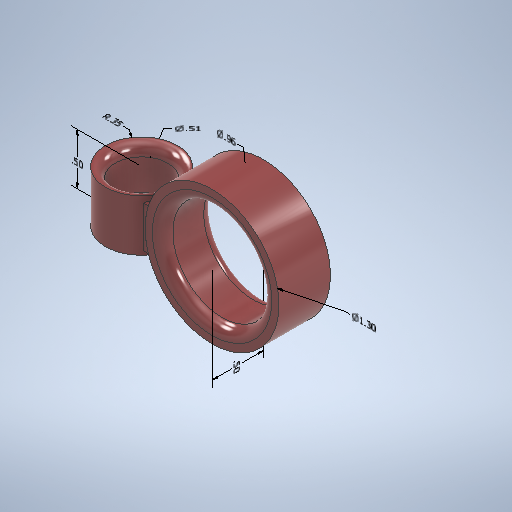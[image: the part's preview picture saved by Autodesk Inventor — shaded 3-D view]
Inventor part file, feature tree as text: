
AUTODESK INVENTOR PART (.ipt)
format: ipt  version: 2025.2 (Build 292293000, 293)  size: 366,592 bytes
history: native  units: in
note: dims shown in document units (in); Inventor stores cm internally (conversion verified against a paired STEP export)
features: other x7, sketch x4, extrude x3, plane x2, fillet x1
ambient origin geometry x8: Origin, YZ Plane, XZ Plane, XY Plane, X Axis, Y Axis, Z Axis, Center Point
bodies: Solid1 (feature_tree)
feature tree (17):
  other  "Annotations"
  extrude  "Extrusion1"  Depth=0.7in
  plane  "Work Plane1"
  sketch  "Sketch2"  dims[d2=0.5in d3=0.0in d4=1.0in d5=0.35in]
  plane  "Work Plane3"
  extrude  "Extrusion2"  Depth=0.35in
  fillet  "Fillet1"  Radius=0.35in
  extrude  "Extrusion3"  Depth=0.5in
  sketch  "Sketch1"  dims[d0=0.51in d1=0.7in]
  sketch  "Sketch5"  dims[d6=0.5in d7=0.5in]
  sketch  "Sketch6"  dims[d8=90.0deg d10=0.96in d11=0.25in d12=1.3in d13=0.5in d14=0.0in d15=0.1in d16=0.4in d17=0.0in d18=-0.57in d19=0.96in d20=0.5in d21=0.0811in d22=1.3in d23=0.7183in d24=0.51in d25=0.5in d26=2.239in d27=0.35in]
  other  "Diameter Dimension 1"
  other  "Linear Dimension 1"
  other  "Diameter Dimension 2"
  other  "Diameter Dimension 3"
  other  "Linear Dimension 2"
  other  "Radial Dimension 1"
